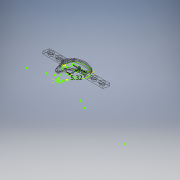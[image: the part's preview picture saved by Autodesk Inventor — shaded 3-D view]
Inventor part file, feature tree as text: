
AUTODESK INVENTOR PART (.ipt)
format: ipt  version: 2018 (Build 220112000, 112)  size: 2,423,808 bytes
history: native  units: mm
features: sketch x64, extrude x59, fillet x30, mirror x3, shell x1, hole x1
ambient origin geometry x8: Origin, YZ Plane, XZ Plane, XY Plane, X Axis, Y Axis, Z Axis, Center Point
bodies: Solid1 (feature_tree)
feature tree (158):
  extrude  "Extrusion1"  TaperAngle=0.0deg  [1 undecoded]
  extrude  "Extrusion2"  Depth=10.0mm
  extrude  "Extrusion3"  TaperAngle=0.0deg  [1 undecoded]
  shell  "Shell2"  Thickness=0.0mm
  extrude  "Extrusion4"  Depth=1.6mm
  extrude  "Extrusion6"  Depth=10.0mm TaperAngle=0.0deg
  extrude  "Extrusion7"  Depth=1.75mm
  extrude  "Extrusion8"  Depth=2.0mm
  extrude  "Extrusion9"  Depth=10.0mm TaperAngle=0.0deg
  extrude  "Extrusion11"  Depth=10.0mm TaperAngle=0.0deg
  fillet  "Fillet1"  Radius=10.0mm
  fillet  "Fillet2"  Radius=10.0mm
  fillet  "Fillet3"  [1 undecoded]
  fillet  "Fillet4"  Radius=0.541mm
  fillet  "Fillet5"  [1 undecoded]
  extrude  "Extrusion12"  Depth=7.5mm TaperAngle=0.0deg
  extrude  "Extrusion13"  TaperAngle=0.0deg  [1 undecoded]
  extrude  "Extrusion16"  Depth=51.0mm TaperAngle=0.0deg
  extrude  "Extrusion17"  TaperAngle=0.0deg  [1 undecoded]
  extrude  "Extrusion18"  Depth=10.0mm TaperAngle=0.0deg
  extrude  "Extrusion19"  Depth=10.0mm TaperAngle=0.0deg
  fillet  "Fillet6"  Radius=6.0mm
  extrude  "Extrusion20"  Depth=42.0mm TaperAngle=0.0deg
  fillet  "Fillet7"  Radius=42.0mm
  extrude  "Extrusion21"  Depth=2.6mm
  extrude  "Extrusion22"  Depth=2.6mm
  sketch  "Sketch23"  dims[d147=12.0125mm d148=12.0125mm]
  extrude  "Extrusion24"  Depth=12.0125mm
  extrude  "Extrusion26"  Depth=17.5mm
  extrude  "Extrusion28"  Depth=3.0mm
  extrude  "Extrusion32"  Depth=3.0mm
  extrude  "Extrusion37"  Depth=2.0mm TaperAngle=0.0deg
  extrude  "Extrusion38"  Depth=10.0mm TaperAngle=0.0deg
  extrude  "Extrusion40"  Depth=3.11mm
  extrude  "Extrusion41"  Depth=10.0mm TaperAngle=0.0deg
  extrude  "Extrusion42"  Depth=0.365mm TaperAngle=0.0deg
  extrude  "Extrusion43"  TaperAngle=0.0deg  [1 undecoded]
  extrude  "Extrusion44"  TaperAngle=0.0deg  [1 undecoded]
  hole  "Hole1"  [1 undecoded]
  sketch  "Sketch45"  dims[d203=20.0mm d204=15.65mm d205=0.0mm]
  extrude  "Extrusion45"  Depth=15.65mm TaperAngle=0.0deg
  extrude  "Extrusion47"  Depth=0.861mm
  mirror  "Mirror1"
  extrude  "Extrusion48"  Depth=1.61mm
  fillet  "Fillet23"  [1 undecoded]
  fillet  "Fillet24"  Radius=1.92mm
  extrude  "Extrusion49"  Depth=0.276mm
  extrude  "Extrusion50"  TaperAngle=0.0deg  [1 undecoded]
  extrude  "Extrusion54"  TaperAngle=0.0deg  [1 undecoded]
  extrude  "Extrusion55"  Depth=2.5mm
  extrude  "Extrusion56"  TaperAngle=0.0deg  [1 undecoded]
  extrude  "Extrusion57"  Depth=10.0mm TaperAngle=0.0deg
  sketch  "Sketch61"  dims[d255=2.57mm d256=2.37mm]
  extrude  "Extrusion58"  Depth=0.83mm TaperAngle=0.0deg
  extrude  "Extrusion59"  Depth=2.37mm
  extrude  "Extrusion60"  Depth=4.5mm
  fillet  "Fillet27"  Radius=0.83mm
  fillet  "Fillet28"  Radius=6.37mm
  extrude  "Extrusion61"  Depth=2.0mm TaperAngle=0.0deg
  fillet  "Fillet29"  Radius=6.71mm
  fillet  "Fillet30"  Radius=6.71mm
  fillet  "Fillet31"  [1 undecoded]
  fillet  "Fillet32"  Radius=2.0mm
  extrude  "Extrusion62"  Depth=2.0mm
  fillet  "Fillet33"  Radius=2.0mm
  fillet  "Fillet34"  Radius=2.0mm
  fillet  "Fillet35"  Radius=2.0mm
  fillet  "Fillet36"  Radius=2.0mm
  extrude  "Extrusion63"  [1 undecoded]
  extrude  "Extrusion64"  [1 undecoded]
  extrude  "Extrusion65"  [1 undecoded]
  fillet  "Fillet37"  [1 undecoded]
  fillet  "Fillet38"  [1 undecoded]
  extrude  "Extrusion69"  [1 undecoded]
  extrude  "Extrusion70"  [1 undecoded]
  extrude  "Extrusion71"  [1 undecoded]
  extrude  "Extrusion72"  [1 undecoded]
  extrude  "Extrusion73"  [1 undecoded]
  extrude  "Extrusion74"  [1 undecoded]
  fillet  "Fillet42"  [1 undecoded]
  fillet  "Fillet43"  [1 undecoded]
  extrude  "Extrusion75"  [1 undecoded]
  extrude  "Extrusion76"  [1 undecoded]
  mirror  "Mirror2"
  extrude  "Extrusion77"  [1 undecoded]
  extrude  "Extrusion78"  [1 undecoded]
  extrude  "Extrusion79"  [1 undecoded]
  mirror  "Mirror3"
  extrude  "Extrusion80"  [1 undecoded]
  extrude  "Extrusion81"  [1 undecoded]
  fillet  "Fillet44"  [1 undecoded]
  fillet  "Fillet45"  [1 undecoded]
  fillet  "Fillet46"  [1 undecoded]
  fillet  "Fillet47"  [1 undecoded]
  fillet  "Fillet48"  [1 undecoded]
  fillet  "Fillet49"  [1 undecoded]
  fillet  "Fillet50"  [1 undecoded]
  sketch  "Sketch86"
  sketch  "Sketch87"
  sketch  "Sketch1"  dims[d0=10.0mm d1=0.0mm d4=0.0mm d5=0.0mm]
  sketch  "Sketch2"  dims[d6=10.0mm d7=0.0mm d9=1.2mm]
  sketch  "Sketch3"  dims[d10=0.0mm d11=0.0mm d14=0.0mm d15=0.0mm d16=0.0mm d17=0.0mm]
  sketch  "Sketch4"  dims[d18=0.0mm d19=0.0mm d20=1.6mm]
  sketch  "Sketch6"  dims[d21=0.0mm d22=0.0mm d25=10.0mm d26=0.0mm]
  sketch  "Sketch7"  dims[d27=2.23mm d28=1.75mm]
  sketch  "Sketch8"  dims[d29=2.79mm d30=2.0mm]
  sketch  "Sketch9"  dims[d31=5.19mm d32=10.0mm d33=0.0mm]
  sketch  "Sketch11"  dims[d34=10.0mm d35=0.0mm d40=10.0mm d41=0.0mm d42=10.0mm d43=0.0mm d44=10.0mm d45=0.0mm d46=0.0mm d47=0.0mm d48=0.541mm d49=0.0mm d50=0.0mm]
  sketch  "Sketch12"  dims[d51=4.84mm d52=7.5mm d53=0.0mm]
  sketch  "Sketch13"  dims[d54=0.0mm d55=0.0mm d59=0.0mm d60=0.0mm]
  sketch  "Sketch16"  dims[d78=51.0mm d79=0.0mm d84=51.0mm d85=0.0mm]
  sketch  "Sketch17"  dims[d94=51.0mm d95=0.0mm d123=0.0mm d124=0.0mm]
  sketch  "Sketch18"  dims[d125=0.0mm d126=0.0mm d131=10.0mm d132=0.0mm]
  sketch  "Sketch19"  dims[d133=10.0mm d134=0.0mm d135=10.0mm d136=0.0mm d137=6.0mm]
  sketch  "Sketch20"  dims[d138=1.9mm d139=42.0mm d140=0.0mm d141=42.0mm d142=0.0mm]
  sketch  "Sketch21"  dims[d143=2.6mm d144=2.6mm]
  sketch  "Sketch22"  dims[d145=2.6mm d146=2.6mm]
  sketch  "Sketch24"  dims[d149=17.5mm d150=17.5mm]
  sketch  "Sketch26"  dims[d151=3.0mm d152=3.0mm]
  sketch  "Sketch28"  dims[d153=3.0mm d154=3.0mm]
  sketch  "Sketch32"  dims[d155=2.6mm d156=6.0mm d157=4.4mm d158=2.0mm d159=14.3117mm d160=8.0mm d161=20.594885mm d162=12.0mm d163=0.0mm]
  sketch  "Sketch37"  dims[d170=10.0mm d171=0.0mm d172=10.0mm d173=0.0mm]
  sketch  "Sketch38"  dims[d174=3.64mm d175=3.11mm]
  sketch  "Sketch40"  dims[d176=0.0mm d177=0.0mm d178=10.0mm d179=0.0mm]
  sketch  "Sketch41"  dims[d186=0.365mm d187=0.0mm d190=0.365mm d191=0.0mm]
  sketch  "Sketch42"  dims[d192=0.0mm d193=0.0mm d194=0.0mm d195=0.0mm]
  sketch  "Sketch43"  dims[d196=0.0mm d197=0.0mm d198=0.0mm d199=0.0mm]
  sketch  "Sketch44"  dims[d200=0.0mm d201=0.0mm d202=2.0mm]
  sketch  "Sketch46"  dims[d206=0.675mm d207=0.861mm]
  sketch  "Sketch48"  dims[d208=0.8mm d209=1.61mm d210=0.0mm d211=0.0mm d212=1.92mm]
  sketch  "Sketch49"  dims[d213=2.91mm d214=0.276mm]
  sketch  "Sketch50"  dims[d215=0.425mm d218=0.0mm d219=0.0mm]
  sketch  "Sketch51"  dims[d222=10.0mm d223=0.0mm d226=0.0mm d227=0.0mm]
  sketch  "Sketch55"  dims[d228=5.04mm d229=2.5mm]
  sketch  "Sketch57"  dims[d241=10.0mm d242=0.0mm d245=0.0mm d246=0.0mm]
  sketch  "Sketch59"  dims[d247=10.0mm d248=0.0mm d249=1.22mm d250=0.0mm]
  sketch  "Sketch60"  dims[d251=0.0mm d252=0.0mm d253=0.83mm d254=0.0mm]
  sketch  "Sketch62"  dims[d257=9.0mm d258=5.320111mm d259=8.0mm d260=4.5mm d261=0.83mm d262=0.0mm d263=6.37mm d264=0.0mm]
  sketch  "Sketch63"  dims[d265=6.37mm d266=0.0mm d267=6.37mm d268=0.0mm d269=6.71mm d270=0.0mm d271=6.71mm d272=0.0mm d273=0.0mm d274=0.0mm d275=2.0mm]
  sketch  "Sketch64"  dims[d276=0.789mm d277=2.0mm d278=2.0mm d279=2.0mm d280=2.0mm d281=2.0mm]
  sketch  "Sketch65"  dims[d282=9.0mm d283=5.320111mm d284=8.0mm]
  sketch  "Sketch66"
  sketch  "Sketch67"
  sketch  "Sketch68"
  sketch  "Sketch69"
  sketch  "Sketch73"
  sketch  "Sketch74"
  sketch  "Sketch75"
  sketch  "Sketch76"
  sketch  "Sketch77"
  sketch  "Sketch78"
  sketch  "Sketch79"
  sketch  "Sketch80"
  sketch  "Sketch81"
  sketch  "Sketch82"
  sketch  "Sketch83"
  sketch  "Sketch84"
  sketch  "Sketch85"
note: 41 required parameter values undecoded (feature->parameter linkage not recoverable at this tier; creation-order binding heuristic only, values carry confidence <= 0.55)
